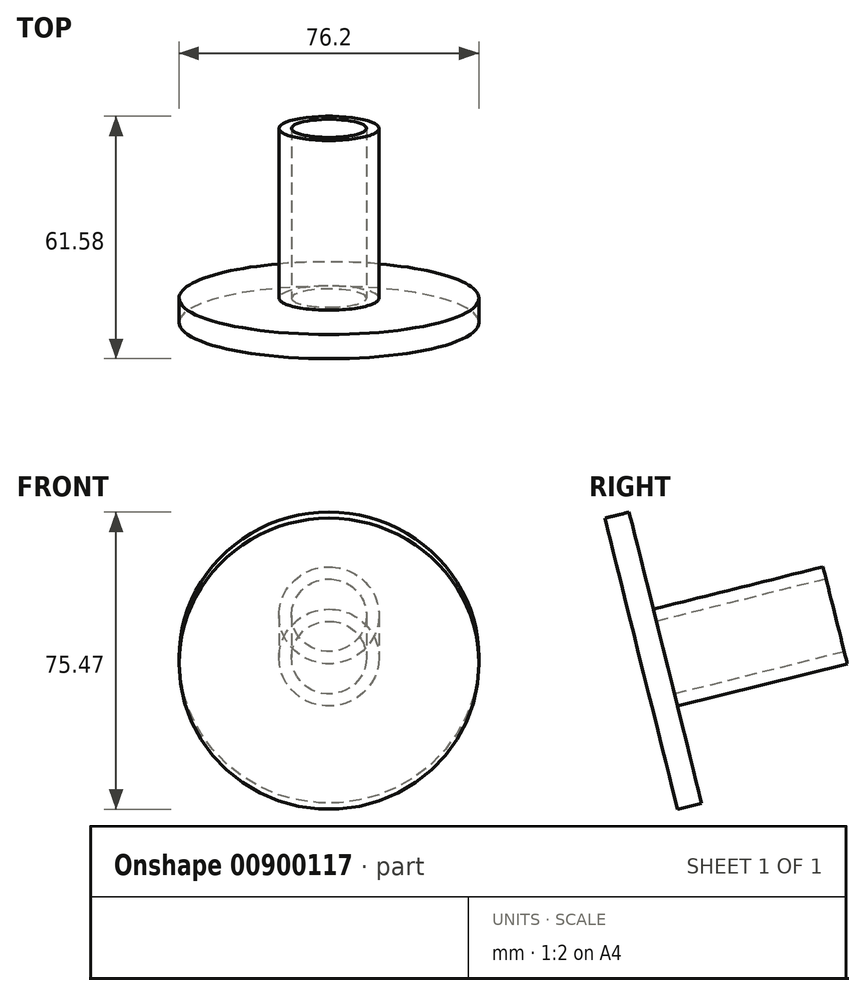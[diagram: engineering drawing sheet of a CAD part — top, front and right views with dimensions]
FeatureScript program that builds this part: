
annotation { "Feature Type Name" : "Feature", "Feature Type Description" : "" }
export const myFeature = defineFeature(function(context is Context, id is Id, definition is map)
    precondition{}
    {
        {
            var Q0;
            Q0=qCreatedBy(makeId("Top.planeOp"),FACE);
            var sketch = newSketch(context, id + "F0", { "sketchPlane" : qUnion([Q0])});
            skLineSegment(sketch, "E0", {"start": v(-53.26, 0) * mm, "end": v(35.2, 0) * mm});
            skSolve(sketch);
        }
        {
            var Q0;
            Q0=sQuery(id+"F0.wireOp",EDGE,"E0");
            cPlane(context, id + "F1", {"entities" : qUnion([Q0]), "cplaneType" : CPlaneType.LINE_ANGLE, "offset" : 25.4 * mm, "angle" : 14 * degree, "width" : 152.4 * mm, "height" : 152.4 * mm});
        }
        {
            var Q0;
            Q0=qCreatedBy(id+"F1.planeOp",FACE);
            var sketch = newSketch(context, id + "F2", { "sketchPlane" : qUnion([Q0])});
            skCircle(sketch, "E1", {"center": v(0, 0) * mm, "radius": 38.1 * mm});
            skSolve(sketch);
        }
        {
            var Q0;
            Q0=makeQuery(id+"F2.imprint","IMPRINT",FACE,{"disambiguationData":[TD([[makeQuery(id+"F2.imprint","IMPRINT",EDGE,{"derivedFrom":sQuery(id+"F2.wireOp",EDGE,"E1")}),1.0]])]});
            extrude(context, id + "F3", {"entities" : qUnion([Q0]), "depth" : 6.35 * mm, "offsetDistance" : 25.4 * mm});
        }
        {
            var Q0;
            Q0=qCreatedBy(id+"F1.planeOp",FACE);
            var sketch = newSketch(context, id + "F4", { "sketchPlane" : qUnion([Q0])});
            skLineSegment(sketch, "E2", {"start": v(0, 0) * mm, "end": v(0, -23.54) * mm});
            skSolve(sketch);
        }
        {
            var Q0;
            Q0=sQuery(id+"F4.wireOp",EDGE,"E2");
            cPlane(context, id + "F5", {"entities" : qUnion([Q0]), "cplaneType" : CPlaneType.LINE_ANGLE, "offset" : 25.4 * mm, "angle" : 90 * degree, "width" : 152.4 * mm, "height" : 152.4 * mm});
        }
        {
            var Q0;
            Q0=qCreatedBy(id+"F5.planeOp",FACE);
            var sketch = newSketch(context, id + "F6", { "sketchPlane" : qUnion([Q0])});
            skCircle(sketch, "E3", {"center": v(0, 0) * mm, "radius": 12.7 * mm});
            skCircle(sketch, "E4", {"center": v(0, 0) * mm, "radius": 9.53 * mm});
            skSolve(sketch);
        }
        {
            var Q0;
            Q0=qSketchRegion(id+"F6",true);
            extrude(context, id + "F7", {"entities" : qUnion([Q0]), "operationType" : NewBodyOperationType.ADD, "depth" : 50.8 * mm, "offsetDistance" : 25.4 * mm});
        }
        {
            var Q0;
            Q0=qCreatedBy(makeId("Right.planeOp"),FACE);
            var sketch = newSketch(context, id + "F8", { "sketchPlane" : qUnion([Q0])});
            skLineSegment(sketch, "E5", {"start": v(-5.65, 22.67) * mm, "end": v(3.55, -14.24) * mm});
            skLineSegment(sketch, "E6", {"start": v(3.55, -14.24) * mm, "end": v(-9.6, -17.93) * mm});
            skLineSegment(sketch, "E7", {"start": v(-9.6, -17.93) * mm, "end": v(-19.9, 18.75) * mm});
            skLineSegment(sketch, "E8", {"start": v(-19.9, 18.75) * mm, "end": v(-5.65, 22.67) * mm});
            skSolve(sketch);
        }
        {
            var Q0;
            Q0=makeQuery(id+"F8.imprint","IMPRINT",FACE,{"disambiguationData":[TD([[makeQuery(id+"F8.imprint","IMPRINT",EDGE,{"derivedFrom":sQuery(id+"F8.wireOp",EDGE,"E5")}),-1.0]])]});
            extrude(context, id + "F9", {"entities" : qUnion([Q0]), "operationType" : NewBodyOperationType.REMOVE, "oppositeDirection" : true, "depth" : 25.4 * mm, "offsetDistance" : 25.4 * mm});
        }
    });
